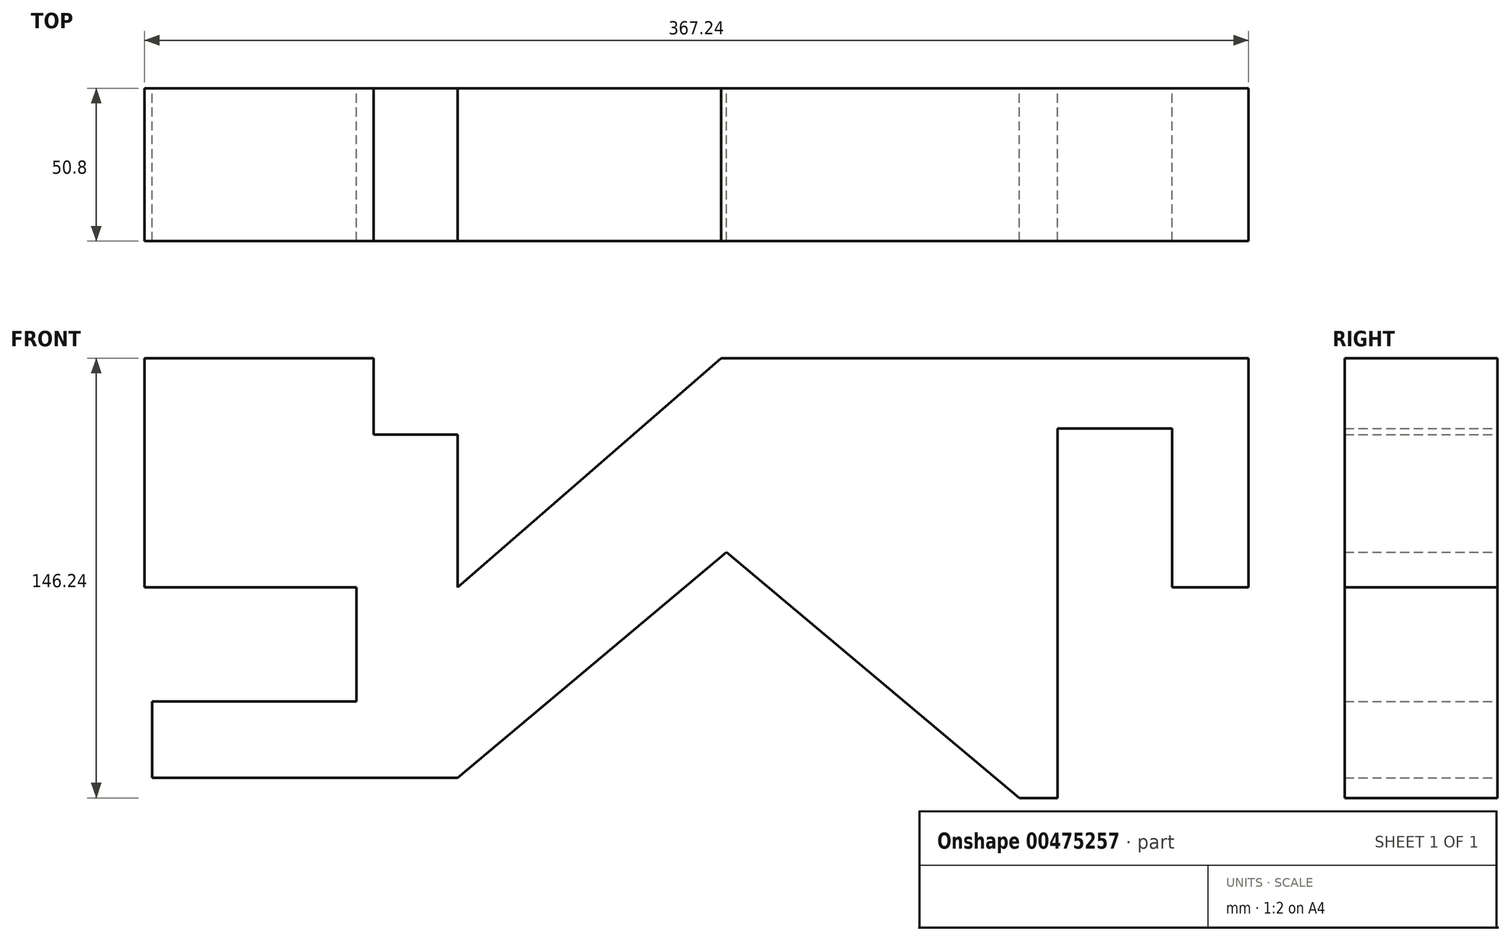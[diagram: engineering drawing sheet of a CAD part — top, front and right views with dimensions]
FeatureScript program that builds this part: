
annotation { "Feature Type Name" : "Feature", "Feature Type Description" : "" }
export const myFeature = defineFeature(function(context is Context, id is Id, definition is map)
    precondition{}
    {
        {
            var Q0;
            Q0=qCreatedBy(makeId("Front.planeOp"),FACE);
            var sketch = newSketch(context, id + "F0", { "sketchPlane" : qUnion([Q0])});
            skLineSegment(sketch, "E0", {"start": v(-104.14, 76.2) * mm, "end": v(-104.14, 0) * mm});
            skLineSegment(sketch, "E1", {"start": v(-104.14, 0) * mm, "end": v(-33.64, 0) * mm});
            skLineSegment(sketch, "E2", {"start": v(-33.64, 0) * mm, "end": v(-33.64, -38.02) * mm});
            skLineSegment(sketch, "E3", {"start": v(-33.64, -38.02) * mm, "end": v(-101.6, -38.02) * mm});
            skLineSegment(sketch, "E4", {"start": v(-101.6, -38.02) * mm, "end": v(-101.6, -63.42) * mm});
            skLineSegment(sketch, "E5", {"start": v(-101.6, -63.42) * mm, "end": v(0, -63.42) * mm});
            skLineSegment(sketch, "E6", {"start": v(186.9, -70.04) * mm, "end": v(199.6, -70.04) * mm});
            skLineSegment(sketch, "E7", {"start": v(199.6, -70.04) * mm, "end": v(199.6, 52.8) * mm});
            skLineSegment(sketch, "E8", {"start": v(199.6, 52.8) * mm, "end": v(237.7, 52.8) * mm});
            skLineSegment(sketch, "E9", {"start": v(237.7, 52.8) * mm, "end": v(237.7, 0) * mm});
            skLineSegment(sketch, "E10", {"start": v(237.7, 0) * mm, "end": v(263.1, 0) * mm});
            skLineSegment(sketch, "E11", {"start": v(263.1, 0) * mm, "end": v(263.1, 76.2) * mm});
            skLineSegment(sketch, "E12", {"start": v(263.1, 76.2) * mm, "end": v(87.66, 76.2) * mm});
            skLineSegment(sketch, "E13", {"start": v(87.66, 76.2) * mm, "end": v(0, 0) * mm});
            skLineSegment(sketch, "E14", {"start": v(0, 0) * mm, "end": v(0, 50.8) * mm});
            skLineSegment(sketch, "E15", {"start": v(0, 50.8) * mm, "end": v(-27.94, 50.8) * mm});
            skLineSegment(sketch, "E16", {"start": v(-27.94, 50.8) * mm, "end": v(-27.94, 76.2) * mm});
            skLineSegment(sketch, "E17", {"start": v(-27.94, 76.2) * mm, "end": v(-104.14, 76.2) * mm});
            skLineSegment(sketch, "E18", {"start": v(0, -63.42) * mm, "end": v(89.5, 11.69) * mm});
            skLineSegment(sketch, "E19", {"start": v(89.5, 11.69) * mm, "end": v(186.9, -70.04) * mm});
            skLineSegment(sketch, "E20", {"start": v(0, -63.42) * mm, "end": v(13.05, -63.42) * mm});
            skLineSegment(sketch, "E21", {"start": v(33.11, -63.42) * mm, "end": v(0, -63.42) * mm});
            skSolve(sketch);
        }
        {
            var Q0;
            Q0=makeQuery(id+"F0.imprint","IMPRINT",FACE,{"disambiguationData":[TD([[makeQuery(id+"F0.imprint","IMPRINT",EDGE,{"derivedFrom":sQuery(id+"F0.wireOp",EDGE,"E0")}),1.0]])]});
            extrude(context, id + "F1", {"entities" : qUnion([Q0]), "depth" : 50.8 * mm});
        }
    });
